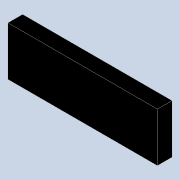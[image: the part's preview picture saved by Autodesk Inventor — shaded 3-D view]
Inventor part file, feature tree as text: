
AUTODESK INVENTOR PART (.ipt)
format: ipt  version: 2021 (Build 250183000, 183)  size: 76,288 bytes
history: native  units: in
note: dims shown in document units (in); Inventor stores cm internally (conversion verified against a paired STEP export)
features: extrude x1, sketch x1
ambient origin geometry x8: Origin, YZ Plane, XZ Plane, XY Plane, X Axis, Y Axis, Z Axis, Center Point
bodies: Solid1 (feature_tree)
feature tree (2):
  extrude  "Extrusion1"  Depth=3.8125in
  sketch  "Sketch1"  dims[d0=0.375in d1=3.8125in d2=1.25in d3=0.0in]
